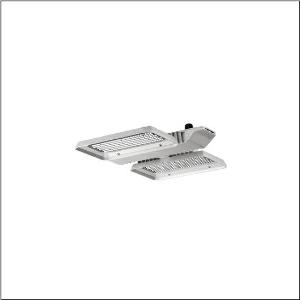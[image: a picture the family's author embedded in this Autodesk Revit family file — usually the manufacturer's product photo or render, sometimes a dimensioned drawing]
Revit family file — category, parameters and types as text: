
# Revit family: highbay_11_51hl62d14dca
name_source: partatom
category: Lighting Fixtures
units: mm (PartAtom-declared; Revit-internal decimal feet)

## family parameters
Cut with Voids When Loaded = No
Host = Face
Light Source = No
Part Type = Normal
Room Calculation Point = No
Round Connector Dimension = Use Diameter
Shared = No

## types (1)
- --- (1 x LED, 10020 lm, 55.6 W, 4000K)
    Apparent Load = 56 VA
    CIE Flux Codes = 89 96 99 100 100
    Color Rendering = 80
    Color Temperature = 4000K
    Default Elevation = 1800 mm
    Description = Highbay 11, LED high bay luminaire, primary light control with lens, of PMMA, light emission: direct distribution, primary light characteristic: symmetric, installation type: surface-mounted, suspended mounting, for 1x 2x LED, rated luminous flux: 10.020lm, luminous efficacy: 180lm/W, light colour: 840, colour temperature: 4000K, control gear: ECG DALI, with terminal, 5-pole, max. 2.5mm², mains connection: 230..240V, AC, 50/60Hz, rated input power: 56W, LED unit, of diecast aluminium, coated, metallic grey (RAL 9006), length: 470mm, width: 500mm, height: 65mm, housing, of diecast aluminium, coated, metallic grey (RAL 9006), protection rating (complete): IP65, insulation class (complete): insulation class I (protective earthing), certification: CE, ENEC, VDE, UKCA, protection symbol: D, impact resistance: IK08 with glass or PC cover, permissible operating ambient temperature: -35..+70°C, corresponds to IFS (International Featured Standards) requirements for safety and quality in the food industry, reducing of maximum allowable ambient temperature of 5°C with ceiling mounting, packaging unit: 1 piece
    Height = 95 mm
    Lamp = 1 x LED
    Lamp Light Flux = 10020 lm
    Lamp Power = 55.6 W
    Lamp count = 1
    Length = 468 mm
    Luminous efficacy = 180 lm/W
    Manufacturer = Siteco
    ModVariant = No
    Model = 51HL62D14DCA
    Mounting Place = Ceiling
    Mounting Type = Pendant
    Number of Poles = 1
    OnlyDefault = Yes
    Power Factor = 1
    Product Name = Highbay 11
    Product group = LED high bay luminaire
    ProductGroupID = 903
    Protection Class = Protection class I
    Protection Degree = IP 65
    RLX_Detail_Level = 1
    RLX_Emergency_Light_Flux = 0 lm
    RLX_Emergency_Type = 0
    RLX_Emergency_Type_DB = No
    RlxData = <blob elided: 71033 chars, md5=b7589056>
    Socket = socket
    Standby Power = 0 W
    System Light Flux = 10020 lm
    System Power = 56 W
    Type Comments = factory setting: luminous flux: 100 % | dim-lin: 254 | 315 mA
    Type Image = l_1003425.jpg
    URL = http://relux.com
    VarID = @adj_159989
    Voltage = 0 V
    Weight = 0.00 kg
    Width = 501 mm

## geometry (parser evidence)
native form markers: Blend x4, Sweep x12
no freeform markers — native parametric forms only
